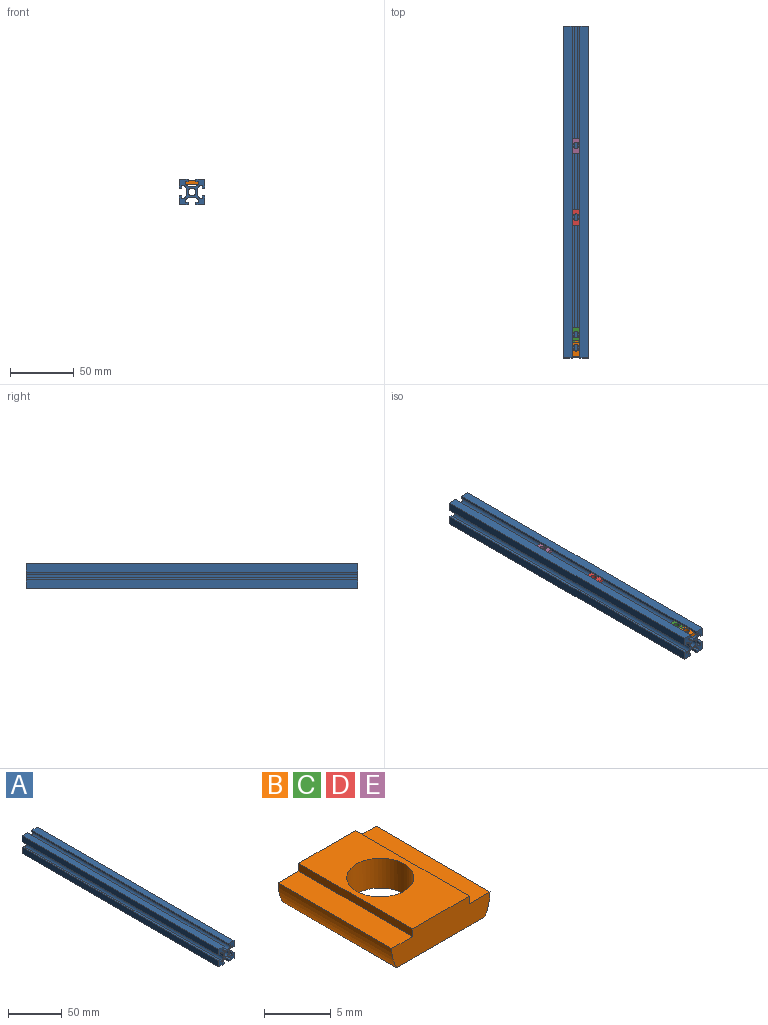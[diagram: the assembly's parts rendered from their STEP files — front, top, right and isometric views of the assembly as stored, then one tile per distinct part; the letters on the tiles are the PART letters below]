
ASSEMBLY  parts=5 mates=4
PART A: 39 faces, bbox 20x260x20 mm
  f0: plane 260x2.19mm, normal (1,0,0), area 568.7mm2, adj f1,f36,f37,f38
  f1: plane 260x2mm, normal (0,0,1), area 520mm2, adj f0,f2,f37,f38
  f2: plane 260x7mm, normal (-1,0,0), area 1820mm2, adj f1,f3,f37,f38
  f3: plane 260x7mm, normal (0,0,-1), area 1820mm2, adj f2,f4,f37,f38
  f4: plane 260x2mm, normal (1,0,0), area 520mm2, adj f3,f5,f37,f38
  f5: plane 260x2.19mm, normal (0,0,1), area 568.7mm2, adj f4,f6,f37,f38
  f6: cylinder r=3.97mm len=260mm, axis (0,1,0), area 1629.7mm2, adj f5,f7,f37,f38
  f7: plane 260x2.43mm, normal (0,0,-1), area 631.3mm2, adj f6,f8,f37,f38
  f8: cylinder r=3.97mm len=260mm, axis (0,1,0), area 1629.7mm2, adj f7,f9,f37,f38
  f9: plane 260x2.19mm, normal (0,0,1), area 568.7mm2, adj f8,f10,f37,f38
  f10: plane 260x2mm, normal (-1,0,0), area 520mm2, adj f9,f11,f37,f38
  f11: plane 260x7mm, normal (0,0,-1), area 1820mm2, adj f10,f12,f37,f38
  f12: plane 260x7mm, normal (1,0,0), area 1820mm2, adj f11,f13,f37,f38
  f13: plane 260x2mm, normal (0,0,1), area 520mm2, adj f12,f14,f37,f38
  f14: plane 260x2.19mm, normal (-1,0,0), area 568.7mm2, adj f13,f15,f37,f38
  f15: cylinder r=3.97mm len=260mm, axis (0,1,0), area 1629.7mm2, adj f14,f16,f37,f38
  f16: plane 260x2.43mm, normal (1,0,0), area 631.3mm2, adj f15,f17,f37,f38
  f17: cylinder r=3.97mm len=260mm, axis (0,1,0), area 1629.7mm2, adj f16,f18,f37,f38
  f18: plane 260x2.19mm, normal (-1,0,0), area 568.7mm2, adj f17,f19,f37,f38
  f19: plane 260x2mm, normal (0,0,-1), area 520mm2, adj f18,f20,f37,f38
  f20: plane 260x7mm, normal (1,0,0), area 1820mm2, adj f19,f21,f37,f38
  f21: plane 260x7mm, normal (0,0,1), area 1820mm2, adj f20,f22,f37,f38
  f22: plane 260x2mm, normal (-1,0,0), area 520mm2, adj f21,f23,f37,f38
  f23: plane 260x2.19mm, normal (0,0,-1), area 568.7mm2, adj f22,f24,f37,f38
  f24: cylinder r=3.97mm len=260mm, axis (0,1,0), area 1629.7mm2, adj f23,f25,f37,f38
  f25: plane 260x2.43mm, normal (0,0,1), area 631.3mm2, adj f24,f26,f37,f38
  f26: cylinder r=3.97mm len=260mm, axis (0,1,0), area 1629.7mm2, adj f25,f27,f37,f38
  f27: plane 260x2.19mm, normal (0,0,-1), area 568.7mm2, adj f26,f28,f37,f38
  f28: plane 260x2mm, normal (1,0,0), area 520mm2, adj f27,f29,f37,f38
  f29: plane 260x7mm, normal (0,0,1), area 1820mm2, adj f28,f30,f37,f38
  f30: plane 260x7mm, normal (-1,0,0), area 1820mm2, adj f29,f31,f37,f38
  f31: plane 260x2mm, normal (0,0,-1), area 520mm2, adj f30,f32,f37,f38
  f32: plane 260x2.19mm, normal (1,0,0), area 568.7mm2, adj f31,f33,f37,f38
  f33: cylinder r=3.97mm len=260mm, axis (0,1,0), area 1629.7mm2, adj f32,f34,f37,f38
  f34: plane 260x2.43mm, normal (-1,0,0), area 631.3mm2, adj f33,f36,f37,f38
  f35: cylinder r=3mm len=260mm, axis (0,1,0), area 4900.9mm2, adj f37,f38
  f36: cylinder r=3.97mm len=260mm, axis (0,1,0), area 1629.7mm2, adj f0,f34,f37,f38
  f37: plane 20x20mm, normal (0,-1,0), area 184.8mm2, adj f0,f1,f2,f3,f4,f5,f6,f7
  f38: plane 20x20mm, normal (0,1,0), area 184.8mm2, adj f0,f1,f2,f3,f4,f5,f6,f7
PART B: 11 faces, bbox 10.4x12x2.7 mm
  f0: plane 12x9.29mm, normal (0,0,-1), area 91.9mm2, adj f1,f7,f8,f9,f10
  f1: cylinder r=3.97mm len=12mm, axis (0,1,0), area 25.5mm2, adj f0,f2,f8,f9
  f2: plane 12x2.19mm, normal (0,0,1), area 26.2mm2, adj f1,f3,f8,f9
  f3: plane 12x0.7mm, normal (1,0,0), area 8.4mm2, adj f2,f4,f8,f9
  f4: plane 12x6mm, normal (0,0,1), area 52.4mm2, adj f3,f5,f8,f9,f10
  f5: plane 12x0.7mm, normal (-1,0,0), area 8.4mm2, adj f4,f6,f8,f9
  f6: plane 12x2.19mm, normal (0,0,1), area 26.2mm2, adj f5,f7,f8,f9
  f7: cylinder r=3.97mm len=12mm, axis (0,1,0), area 25.5mm2, adj f0,f6,f8,f9
  f8: plane 10.37x2.73mm, normal (0,-1,0), area 24.5mm2, adj f0,f1,f2,f3,f4,f5,f6,f7
  f9: plane 10.37x2.73mm, normal (0,1,0), area 24.5mm2, adj f0,f1,f2,f3,f4,f5,f6,f7
  f10: cylinder r=2.5mm len=5mm, axis (0,0,1), area 42.9mm2, adj f0,f4
PART C: same geometry as B
PART D: same geometry as B
PART E: same geometry as B
PLACE A t=(-69.18,194.37,-27.81)mm
PLACE B t=(-69.18,297.89,-27.81)mm
PLACE C t=(-69.18,308.17,-27.81)mm
PLACE D t=(-69.18,400.31,-27.81)mm
PLACE E t=(-69.18,456.54,-27.81)mm
MATE slider A.f37 <-> E.f8  axis (0,-1,0) through (-66.18,-65.63,-19.81)mm
MATE slider A.f37 <-> C.f8  axis (0,-1,0) through (-66.18,-65.63,-19.81)mm
MATE slider A.f37 <-> B.f8  axis (0,-1,0) through (-66.18,-65.63,-19.81)mm
MATE slider A.f37 <-> D.f8  axis (0,-1,0) through (-66.18,-65.63,-19.81)mm
